# Revit family: sil_silencer
name_source: partatom
category: Duct Accessories
revit_build: Autodesk Revit 2015 (Build: 20140606_1530(x64)
units: mm (PartAtom-declared; Revit-internal decimal feet)

## types (8) — shared parameters
Catalogue Pages = http://www.nuaire.info
Classification.Uniclass.Pr.Description = Sound attenuators
Classification.Uniclass.Pr.Number = Pr_65_67_78
Description = Inline Silencer
Fax Number = +44(0)2920-858-222
IFCExportAs = IfcDuctSilencerType
Manufacturer = Nuaire
Manufacturer Name = Nuaire
OmniClass Number = 23-33 49 21 17
OmniClass Title = Ductwork Sound Attenuators
Postcode = CF83 1NA
Revit Family Last Revised = 30/10/18
Telephone Number = +44(0)2920-858-200
URL = http://www.nuaire.co.uk
Unit Description = Inline Silencer
VAT Registration Number = 877308
Warranty Period = 3 Years
Weatherproof or Internal Only = Internal

## per-type parameters (varying)
| type | Height | Length | Spigot Diameter | Spigot ID | Spigot Radius | Weight | Width |
| SIL-100 | 159 mm  [stored 0.521654 ft] | 600 mm | 100 mm  [stored 0.328084 ft] | 95 mm | 50 mm  [stored 0.164042 ft] | 4.90 kg | 230 mm  [stored 0.754593 ft] |
| SIL-125 | 159 mm  [stored 0.521654 ft] | 600 mm | 125 mm  [stored 0.410105 ft] | 120 mm | 63 mm | 4.90 kg | 230 mm  [stored 0.754593 ft] |
| SIL-150 | 184 mm  [stored 0.603675 ft] | 600 mm | 150 mm | 145 mm | 75 mm | 6.60 kg | 300 mm |
| SIL-200 | 234 mm  [stored 0.767717 ft] | 600 mm | 200 mm  [stored 0.656168 ft] | 195 mm  [stored 0.639764 ft] | 100 mm  [stored 0.328084 ft] | 9.90 kg | 350 mm  [stored 1.14829 ft] |
| SIL-250 | 284 mm  [stored 0.931759 ft] | 600 mm | 250 mm  [stored 0.82021 ft] | 245 mm  [stored 0.803806 ft] | 125 mm  [stored 0.410105 ft] | 10.90 kg | 350 mm  [stored 1.14829 ft] |
| SIL-315 | 349 mm  [stored 1.14501 ft] | 600 mm | 315 mm  [stored 1.03346 ft] | 310 mm  [stored 1.01706 ft] | 158 mm | 12.20 kg | 400 mm  [stored 1.31234 ft] |
| SIL-400 | 475 mm  [stored 1.5584 ft] | 900 mm  [stored 2.95276 ft] | 400 mm  [stored 1.31234 ft] | 395 mm  [stored 1.29593 ft] | 200 mm  [stored 0.656168 ft] | 31.70 kg | 700 mm  [stored 2.29659 ft] |
| SIL-500 | 575 mm | 900 mm  [stored 2.95276 ft] | 500 mm  [stored 1.64042 ft] | 495 mm  [stored 1.62402 ft] | 250 mm  [stored 0.82021 ft] | 40.00 kg | 700 mm  [stored 2.29659 ft] |

note: column(s) folded — value = type name in every type: Model, Nuaire Model Code

note: [stored X ft] marks values corroborated as IEEE doubles in the binary element streams (Revit-internal decimal feet)

## geometry (parser evidence)
native form markers: Blend x4, Sweep x13
no freeform markers — native parametric forms only
